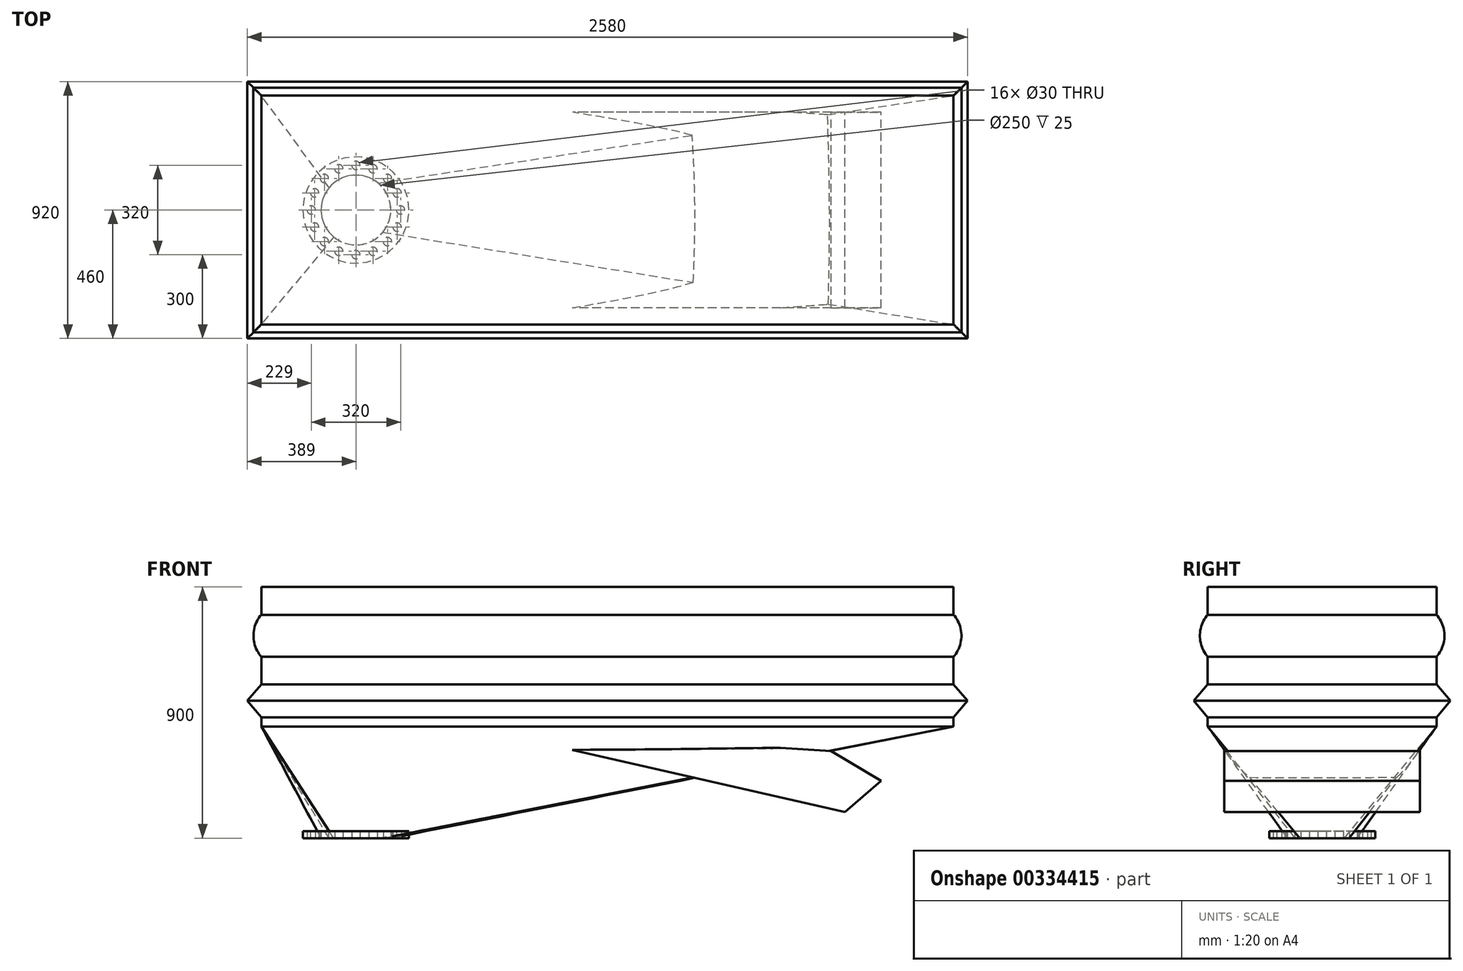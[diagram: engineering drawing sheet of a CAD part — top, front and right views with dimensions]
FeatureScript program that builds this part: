
annotation { "Feature Type Name" : "Feature", "Feature Type Description" : "" }
export const myFeature = defineFeature(function(context is Context, id is Id, definition is map)
    precondition{}
    {
        {
            var Q0;
            Q0=qCreatedBy(makeId("Front.planeOp"),FACE);
            var sketch = newSketch(context, id + "F0", { "sketchPlane" : qUnion([Q0])});
            skLineSegment(sketch, "E0.bottom", {"start": v(1290, -250) * mm, "end": v(-1290, -250) * mm});
            skLineSegment(sketch, "E0.top", {"start": v(1290, 250) * mm, "end": v(-1290, 250) * mm});
            skLineSegment(sketch, "E0.left", {"start": v(1290, -250) * mm, "end": v(1290, 250) * mm});
            skLineSegment(sketch, "E0.right", {"start": v(-1290, -250) * mm, "end": v(-1290, 250) * mm});
            skPoint(sketch, "E0.middle", {"position": v(0, 0) * mm});
            skSolve(sketch);
        }
        {
            var Q0;
            Q0=makeQuery(id+"F0.imprint","IMPRINT",FACE,{"disambiguationData":[TD([[makeQuery(id+"F0.imprint","IMPRINT",EDGE,{"derivedFrom":sQuery(id+"F0.wireOp",EDGE,"E0.bottom")}),-1.0]])]});
            extrude(context, id + "F1", {"entities" : qUnion([Q0]), "endBound" : BoundingType.SYMMETRIC, "depth" : 950 * mm});
        }
        {
            var Q0;
            Q0=makeQuery(id+"F1.opExtrude","CAP_FACE",FACE,{"disambiguationData":[OSD([sQuery(id+"F0.wireOp",EDGE,"E0.bottom"),sQuery(id+"F0.wireOp",EDGE,"E0.top"),sQuery(id+"F0.wireOp",EDGE,"E0.left"),sQuery(id+"F0.wireOp",EDGE,"E0.right")])],"isStart":false});
            var sketch = newSketch(context, id + "F2", { "sketchPlane" : qUnion([Q0])});
            skLineSegment(sketch, "E1", {"start": v(0, 250) * mm, "end": v(0, -250) * mm, "construction": true});
            skLineSegment(sketch, "E2", {"start": v(-1240, 250) * mm, "end": v(-1240, 150.2) * mm});
            skArc(sketch, "E3", {"start": v(-1240, 150.2) * mm, "mid": v(-1268.19, 75.1) * mm, "end": v(-1240, 0) * mm});
            skLineSegment(sketch, "E4", {"start": v(-1290, -158.33) * mm, "end": v(-1240, -99.8) * mm});
            skLineSegment(sketch, "E5", {"start": v(-1290, -158.33) * mm, "end": v(-1240, -216.87) * mm});
            skLineSegment(sketch, "E6.bottom", {"start": v(-1240, 361.69) * mm, "end": v(-1458.32, 361.69) * mm});
            skLineSegment(sketch, "E6.top", {"start": v(-1240, -342.27) * mm, "end": v(-1458.32, -342.27) * mm});
            skLineSegment(sketch, "E6.left", {"start": v(-1240, 361.69) * mm, "end": v(-1240, 150.2) * mm});
            skLineSegment(sketch, "E6.right", {"start": v(-1458.32, 361.69) * mm, "end": v(-1458.32, -342.27) * mm});
            skLineSegment(sketch, "E7.trimOffspring", {"start": v(-1240, -216.87) * mm, "end": v(-1240, -342.27) * mm});
            skLineSegment(sketch, "E8.trimOffspring", {"start": v(-1240, 0) * mm, "end": v(-1240, -99.8) * mm});
            skLineSegment(sketch, "E9.MirrorCS", {"start": v(1240, 0) * mm, "end": v(1240, -99.8) * mm});
            skLineSegment(sketch, "E10.MirrorCS", {"start": v(1290, -158.33) * mm, "end": v(1240, -99.8) * mm});
            skLineSegment(sketch, "E11.MirrorCS", {"start": v(1290, -158.33) * mm, "end": v(1240, -216.87) * mm});
            skLineSegment(sketch, "E12.MirrorCS", {"start": v(1240, 250) * mm, "end": v(1240, 150.2) * mm});
            skLineSegment(sketch, "E13.MirrorCS", {"start": v(1240, 361.69) * mm, "end": v(1240, 150.2) * mm});
            skLineSegment(sketch, "E14.MirrorCS", {"start": v(1458.32, 361.69) * mm, "end": v(1458.32, -342.27) * mm});
            skLineSegment(sketch, "E15.MirrorCS", {"start": v(1240, -216.87) * mm, "end": v(1240, -342.27) * mm});
            skArc(sketch, "E16.MirrorCS", {"start": v(1240, 150.2) * mm, "mid": v(1268.19, 75.1) * mm, "end": v(1240, 0) * mm});
            skLineSegment(sketch, "E17.MirrorCS", {"start": v(1240, -342.27) * mm, "end": v(1458.32, -342.27) * mm});
            skLineSegment(sketch, "E18.MirrorCS", {"start": v(1240, 361.69) * mm, "end": v(1458.32, 361.69) * mm});
            skSolve(sketch);
        }
        {
            var Q0;
            Q0 = qSketchRegion(id + "F2", true);
            var Q1;
            Q1=makeQuery(id+"F1.opExtrude","CAP_VERTEX",VERTEX,{"disambiguationData":[OSD([sQuery(id+"F0.wireOp",EDGE,"E0.top"),sQuery(id+"F0.wireOp",EDGE,"E0.right")])],"isStart":true});
            extrude(context, id + "F3", {"entities" : qUnion([Q0]), "operationType" : NewBodyOperationType.REMOVE, "endBound" : BoundingType.UP_TO_VERTEX, "oppositeDirection" : true, "endBoundEntityVertex" : qUnion([Q1]), "depth" : 25 * mm});
        }
        {
            var Q0;
            Q0=qCreatedBy(makeId("Right.planeOp"),FACE);
            var sketch = newSketch(context, id + "F4", { "sketchPlane" : qUnion([Q0])});
            skLineSegment(sketch, "E19", {"start": v(0, 250) * mm, "end": v(0, -250) * mm, "construction": true});
            skLineSegment(sketch, "E20", {"start": v(-410, 250) * mm, "end": v(-410, 150.2) * mm});
            skArc(sketch, "E21", {"start": v(-410, 150.2) * mm, "mid": v(-438.18, 75.1) * mm, "end": v(-410, 0) * mm});
            skLineSegment(sketch, "E22", {"start": v(-460, -158.33) * mm, "end": v(-410, -99.8) * mm});
            skLineSegment(sketch, "E23", {"start": v(-460, -158.33) * mm, "end": v(-410, -216.87) * mm});
            skLineSegment(sketch, "E24.bottom", {"start": v(-410, 357.73) * mm, "end": v(-610, 357.73) * mm});
            skLineSegment(sketch, "E24.top", {"start": v(-410, -342.27) * mm, "end": v(-610, -342.27) * mm});
            skLineSegment(sketch, "E24.left", {"start": v(-410, 357.73) * mm, "end": v(-410, 150.2) * mm});
            skLineSegment(sketch, "E24.right", {"start": v(-610, 357.73) * mm, "end": v(-610, -342.27) * mm});
            skLineSegment(sketch, "E25.trimOffspring", {"start": v(-410, -216.87) * mm, "end": v(-410, -342.27) * mm});
            skLineSegment(sketch, "E26.trimOffspring", {"start": v(-410, 0) * mm, "end": v(-410, -99.8) * mm});
            skLineSegment(sketch, "E27.MirrorCS", {"start": v(410, 0) * mm, "end": v(410, -99.8) * mm});
            skLineSegment(sketch, "E28.MirrorCS", {"start": v(460, -158.33) * mm, "end": v(410, -99.8) * mm});
            skLineSegment(sketch, "E29.MirrorCS", {"start": v(460, -158.33) * mm, "end": v(410, -216.87) * mm});
            skLineSegment(sketch, "E30.MirrorCS", {"start": v(410, 250) * mm, "end": v(410, 150.2) * mm});
            skLineSegment(sketch, "E31.MirrorCS", {"start": v(410, 357.73) * mm, "end": v(410, 150.2) * mm});
            skLineSegment(sketch, "E32.MirrorCS", {"start": v(610, 357.73) * mm, "end": v(610, -342.27) * mm});
            skLineSegment(sketch, "E33.MirrorCS", {"start": v(410, -216.87) * mm, "end": v(410, -342.27) * mm});
            skArc(sketch, "E34.MirrorCS", {"start": v(410, 150.2) * mm, "mid": v(438.18, 75.1) * mm, "end": v(410, 0) * mm});
            skLineSegment(sketch, "E35.MirrorCS", {"start": v(410, -342.27) * mm, "end": v(610, -342.27) * mm});
            skLineSegment(sketch, "E36.MirrorCS", {"start": v(410, 357.73) * mm, "end": v(610, 357.73) * mm});
            skSolve(sketch);
        }
        {
            var Q0;
            Q0 = qSketchRegion(id + "F4", true);
            extrude(context, id + "F5", {"entities" : qUnion([Q0]), "operationType" : NewBodyOperationType.REMOVE, "endBound" : BoundingType.SYMMETRIC, "oppositeDirection" : true, "depth" : 5000 * mm});
        }
        {
            var Q0;
            Q0=makeQuery(id+"F1.opExtrude","SWEPT_FACE",FACE,{"disambiguationData":[OSD([sQuery(id+"F0.wireOp",EDGE,"E0.bottom")])]});
            cPlane(context, id + "F6", {"entities" : qUnion([Q0]), "cplaneType" : CPlaneType.OFFSET, "offset" : 400 * mm, "width" : 150 * mm, "height" : 150 * mm});
        }
        {
            var Q0;
            Q0=qCreatedBy(id+"F6.planeOp",FACE);
            var sketch = newSketch(context, id + "F7", { "sketchPlane" : qUnion([Q0])});
            skLineSegment(sketch, "E37", {"start": v(-2011.03, 0) * mm, "end": v(1823.62, 0) * mm, "construction": true});
            skCircle(sketch, "E38", {"center": v(-901, 0) * mm, "radius": 125 * mm});
            skCircle(sketch, "E39.0", {"center": v(-901, 0) * mm, "radius": 190 * mm});
            skCircle(sketch, "E40", {"center": v(-901, 160) * mm, "radius": 15 * mm});
            skLineSegment(sketch, "E41", {"start": v(-901, 0) * mm, "end": v(-901, 233.85) * mm, "construction": true});
            skCircle(sketch, "E42.1.0", {"center": v(-962.23, 147.82) * mm, "radius": 15 * mm});
            skCircle(sketch, "E42.2.0", {"center": v(-1014.14, 113.14) * mm, "radius": 15 * mm});
            skCircle(sketch, "E42.3.0", {"center": v(-1048.82, 61.23) * mm, "radius": 15 * mm});
            skCircle(sketch, "E42.4.0", {"center": v(-1061, 0) * mm, "radius": 15 * mm});
            skCircle(sketch, "E42.5.0", {"center": v(-1048.82, -61.23) * mm, "radius": 15 * mm});
            skCircle(sketch, "E42.6.0", {"center": v(-1014.14, -113.14) * mm, "radius": 15 * mm});
            skCircle(sketch, "E42.7.0", {"center": v(-962.23, -147.82) * mm, "radius": 15 * mm});
            skCircle(sketch, "E42.8.0", {"center": v(-901, -160) * mm, "radius": 15 * mm});
            skCircle(sketch, "E42.9.0", {"center": v(-839.77, -147.82) * mm, "radius": 15 * mm});
            skCircle(sketch, "E42.10.0", {"center": v(-787.86, -113.14) * mm, "radius": 15 * mm});
            skCircle(sketch, "E42.11.0", {"center": v(-753.18, -61.23) * mm, "radius": 15 * mm});
            skCircle(sketch, "E42.12.0", {"center": v(-741, 0) * mm, "radius": 15 * mm});
            skCircle(sketch, "E42.13.0", {"center": v(-753.18, 61.23) * mm, "radius": 15 * mm});
            skCircle(sketch, "E42.14.0", {"center": v(-787.86, 113.14) * mm, "radius": 15 * mm});
            skCircle(sketch, "E42.15.0", {"center": v(-839.77, 147.82) * mm, "radius": 15 * mm});
            skSolve(sketch);
        }
        {
            var Q1;
            Q1=makeQuery(id+"F7.imprint","IMPRINT",FACE,{"disambiguationData":[TD([[makeQuery(id+"F7.imprint","IMPRINT",EDGE,{"derivedFrom":sQuery(id+"F7.wireOp",EDGE,"E38")}),1.0]])]});
            var Q2;
            Q2=makeQuery(id+"F1.opExtrude","SWEPT_FACE",FACE,{"disambiguationData":[OSD([sQuery(id+"F0.wireOp",EDGE,"E0.bottom")])]});
            loft(context, id + "F8", {"operationType" : NewBodyOperationType.ADD, "sheetProfilesArray" : [{ "sheetProfileEntities" : qUnion([Q1]) }, { "sheetProfileEntities" : qUnion([Q2]) }]});
        }
        {
            var Q0;
            Q0 = qSketchRegion(id + "F7", true);
            extrude(context, id + "F9", {"entities" : qUnion([Q0]), "oppositeDirection" : true, "depth" : 25 * mm});
        }
        {
            var Q0;
            Q0=qCreatedBy(makeId("Front.planeOp"),FACE);
            var sketch = newSketch(context, id + "F10", { "sketchPlane" : qUnion([Q0])});
            skLineSegment(sketch, "E43", {"start": v(800.8, -338.5) * mm, "end": v(980, -444.9) * mm});
            skLineSegment(sketch, "E44", {"start": v(980, -444.9) * mm, "end": v(851.37, -556.32) * mm});
            skLineSegment(sketch, "E45", {"start": v(851.37, -556.32) * mm, "end": v(-487.2, -251.7) * mm});
            skLineSegment(sketch, "E46", {"start": v(800.8, -338.5) * mm, "end": v(-487.2, -251.7) * mm});
            skSolve(sketch);
        }
        {
            var Q0;
            Q0 = qSketchRegion(id + "F10", true);
            extrude(context, id + "F11", {"entities" : qUnion([Q0]), "operationType" : NewBodyOperationType.ADD, "endBound" : BoundingType.SYMMETRIC, "depth" : 700 * mm});
        }
        {
            var Q0;
            Q0=makeQuery(id+"F9.opExtrude","SWEPT_BODY",BODY,{"disambiguationData":[OSD([sQuery(id+"F7.wireOp",EDGE,"E38"),sQuery(id+"F7.wireOp",EDGE,"E39.0"),sQuery(id+"F7.wireOp",EDGE,"E40"),sQuery(id+"F7.wireOp",EDGE,"E42.1.0"),sQuery(id+"F7.wireOp",EDGE,"E42.2.0"),sQuery(id+"F7.wireOp",EDGE,"E42.3.0"),sQuery(id+"F7.wireOp",EDGE,"E42.4.0"),sQuery(id+"F7.wireOp",EDGE,"E42.5.0"),sQuery(id+"F7.wireOp",EDGE,"E42.6.0"),sQuery(id+"F7.wireOp",EDGE,"E42.7.0"),sQuery(id+"F7.wireOp",EDGE,"E42.8.0"),sQuery(id+"F7.wireOp",EDGE,"E42.9.0"),sQuery(id+"F7.wireOp",EDGE,"E42.10.0"),sQuery(id+"F7.wireOp",EDGE,"E42.11.0"),sQuery(id+"F7.wireOp",EDGE,"E42.12.0"),sQuery(id+"F7.wireOp",EDGE,"E42.13.0"),sQuery(id+"F7.wireOp",EDGE,"E42.14.0"),sQuery(id+"F7.wireOp",EDGE,"E42.15.0")])]});
            transform(context, id + "F12", {"entities" : qUnion([Q0]), "transformType" : TransformType.TRANSLATION_3D, "dx" : 0 * mm, "dy" : 0 * mm, "dz" : 0 * mm, "makeCopy" : true});
        }
        {
            var Q0;
            Q0=makeQuery(id+"F9.opExtrude","SWEPT_BODY",BODY,{"disambiguationData":[OSD([sQuery(id+"F7.wireOp",EDGE,"E38"),sQuery(id+"F7.wireOp",EDGE,"E39.0"),sQuery(id+"F7.wireOp",EDGE,"E40"),sQuery(id+"F7.wireOp",EDGE,"E42.1.0"),sQuery(id+"F7.wireOp",EDGE,"E42.2.0"),sQuery(id+"F7.wireOp",EDGE,"E42.3.0"),sQuery(id+"F7.wireOp",EDGE,"E42.4.0"),sQuery(id+"F7.wireOp",EDGE,"E42.5.0"),sQuery(id+"F7.wireOp",EDGE,"E42.6.0"),sQuery(id+"F7.wireOp",EDGE,"E42.7.0"),sQuery(id+"F7.wireOp",EDGE,"E42.8.0"),sQuery(id+"F7.wireOp",EDGE,"E42.9.0"),sQuery(id+"F7.wireOp",EDGE,"E42.10.0"),sQuery(id+"F7.wireOp",EDGE,"E42.11.0"),sQuery(id+"F7.wireOp",EDGE,"E42.12.0"),sQuery(id+"F7.wireOp",EDGE,"E42.13.0"),sQuery(id+"F7.wireOp",EDGE,"E42.14.0"),sQuery(id+"F7.wireOp",EDGE,"E42.15.0")])]});
            deleteBodies(context, id + "F13", {"entities" : qUnion([Q0])});
        }
    });
